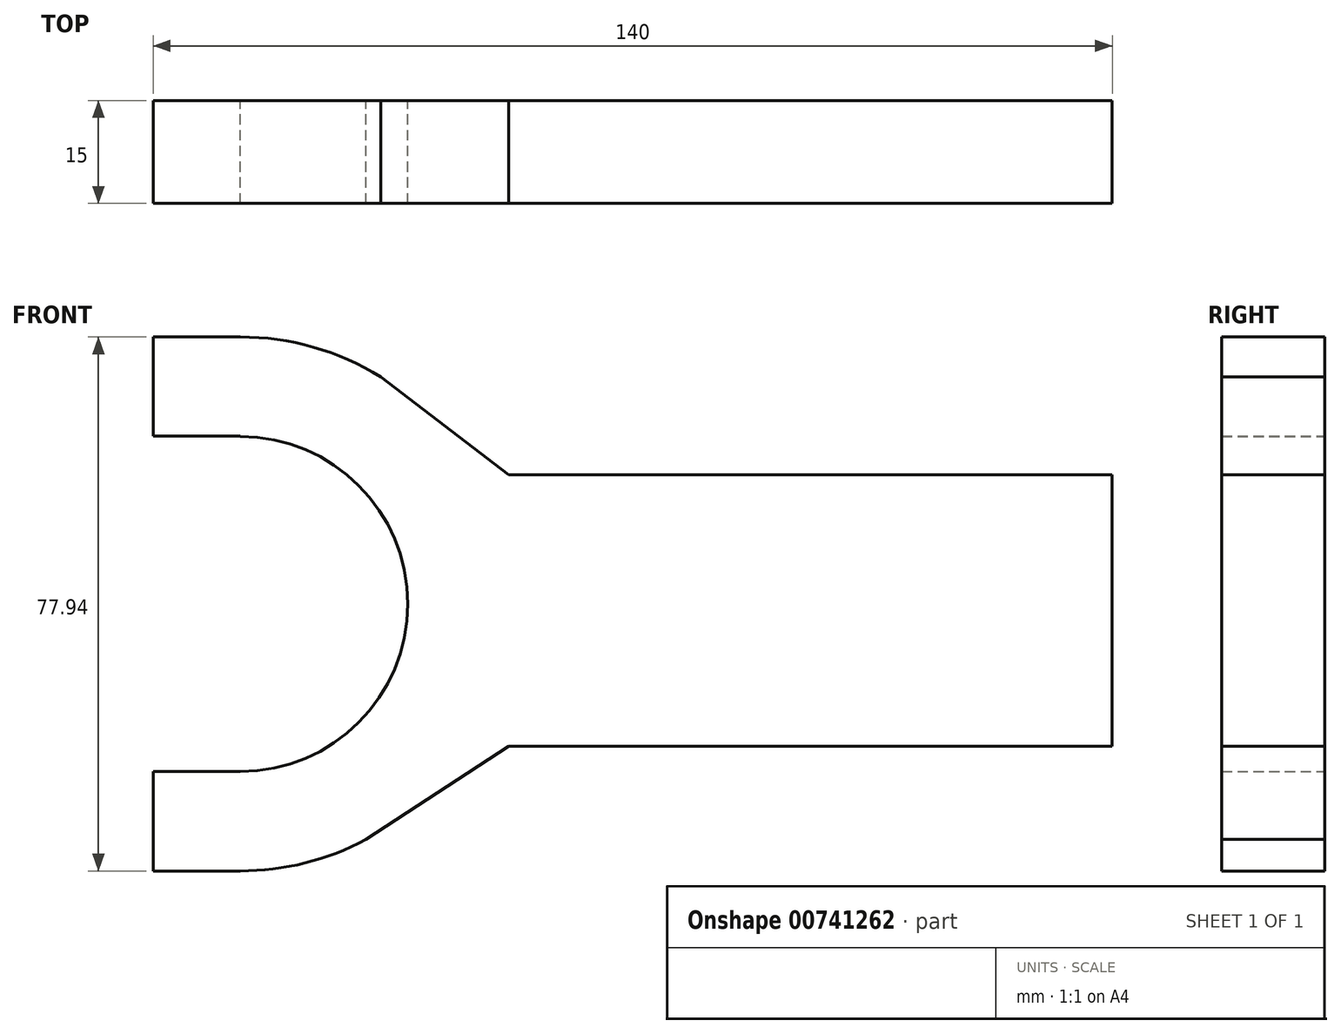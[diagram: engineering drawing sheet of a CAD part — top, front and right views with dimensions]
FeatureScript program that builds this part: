
annotation { "Feature Type Name" : "Feature", "Feature Type Description" : "" }
export const myFeature = defineFeature(function(context is Context, id is Id, definition is map)
    precondition{}
    {
        {
            var Q0;
            Q0=qCreatedBy(makeId("Front.planeOp"),FACE);
            var sketch = newSketch(context, id + "F0", { "sketchPlane" : qUnion([Q0])});
            skArc(sketch, "E0", {"start": v(0, -24.46) * mm, "mid": v(24.46, 0) * mm, "end": v(0, 24.46) * mm});
            skArc(sketch, "E1", {"start": v(0, -38.97) * mm, "mid": v(12.73, -36.83) * mm, "end": v(24.07, -30.65) * mm});
            skLineSegment(sketch, "E2.bottom", {"start": v(39.18, 18.83) * mm, "end": v(127.29, 18.83) * mm});
            skLineSegment(sketch, "E2.top", {"start": v(39.18, -20.8) * mm, "end": v(127.29, -20.8) * mm});
            skLineSegment(sketch, "E2.right", {"start": v(127.29, 18.83) * mm, "end": v(127.29, -20.8) * mm});
            skLineSegment(sketch, "E3", {"start": v(39.18, -20.8) * mm, "end": v(18.36, -34.38) * mm});
            skLineSegment(sketch, "E4", {"start": v(39.18, 18.83) * mm, "end": v(20.49, 33.15) * mm});
            skLineSegment(sketch, "E5", {"start": v(0, 24.53) * mm, "end": v(0, 24.46) * mm});
            skArc(sketch, "E6.trimOffspring", {"start": v(26.68, 28.4) * mm, "mid": v(14.35, 36.23) * mm, "end": v(0, 38.97) * mm});
            skLineSegment(sketch, "E7.bottom", {"start": v(0, -24.46) * mm, "end": v(-12.71, -24.46) * mm});
            skLineSegment(sketch, "E7.top", {"start": v(0, -38.97) * mm, "end": v(-12.71, -38.97) * mm});
            skLineSegment(sketch, "E7.right", {"start": v(-12.71, -24.46) * mm, "end": v(-12.71, -38.97) * mm});
            skLineSegment(sketch, "E8.bottom", {"start": v(0, 38.97) * mm, "end": v(-12.71, 38.97) * mm});
            skLineSegment(sketch, "E8.top", {"start": v(0, 24.53) * mm, "end": v(-12.71, 24.53) * mm});
            skLineSegment(sketch, "E8.right", {"start": v(-12.71, 38.97) * mm, "end": v(-12.71, 24.53) * mm});
            skSolve(sketch);
        }
        {
            var Q0;
            Q0=makeQuery(id+"F0.imprint","IMPRINT",FACE,{"disambiguationData":[TD([[makeQuery(id+"F0.imprint","IMPRINT",EDGE,{"derivedFrom":sQuery(id+"F0.wireOp",EDGE,"E0")}),-1.0]])]});
            extrude(context, id + "F1", {"entities" : qUnion([Q0]), "depth" : 15 * mm, "offsetDistance" : 25 * mm});
        }
    });
